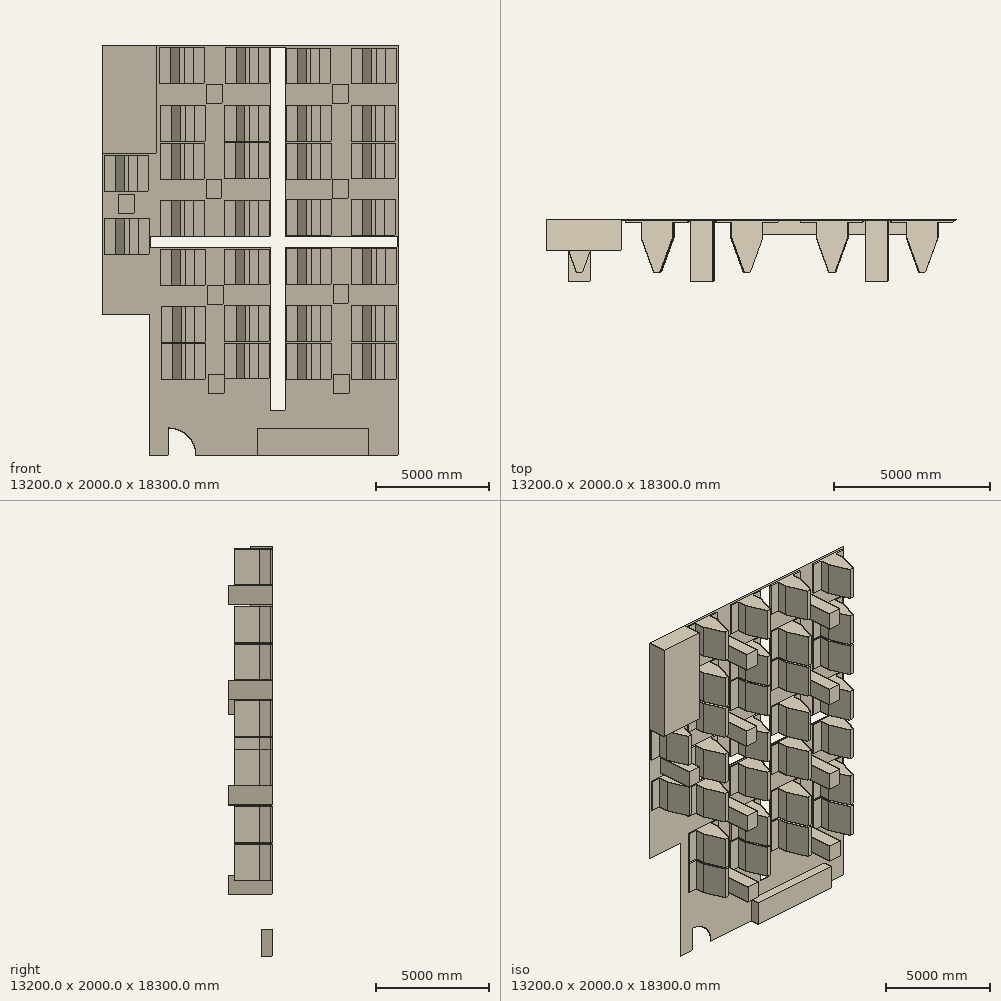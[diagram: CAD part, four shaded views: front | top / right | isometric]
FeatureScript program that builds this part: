
annotation { "Feature Type Name" : "Feature", "Feature Type Description" : "" }
export const myFeature = defineFeature(function(context is Context, id is Id, definition is map)
    precondition{}
    {
        {
            var Q0;
            Q0=qCreatedBy(makeId("Front.planeOp"),FACE);
            var sketch = newSketch(context, id + "F0", { "sketchPlane" : qUnion([Q0])});
            skLineSegment(sketch, "E0.bottom", {"start": v(6600, -7800) * mm, "end": v(-4500, -7800) * mm});
            skLineSegment(sketch, "E0.top", {"start": v(6600, 7800) * mm, "end": v(-6600, 7800) * mm});
            skLineSegment(sketch, "E0.left", {"start": v(6600, -7800) * mm, "end": v(6600, 7800) * mm});
            skLineSegment(sketch, "E0.right", {"start": v(-6600, -4200) * mm, "end": v(-6600, 7800) * mm});
            skPoint(sketch, "E0.middle", {"position": v(0, 0) * mm});
            skLineSegment(sketch, "E1.right", {"start": v(6599.52, -10500) * mm, "end": v(6599.52, -10500.52) * mm});
            skLineSegment(sketch, "E2", {"start": v(-4200, 7800) * mm, "end": v(-4200, 3000) * mm});
            skLineSegment(sketch, "E3", {"start": v(-4200, 3000) * mm, "end": v(-6600, 3000) * mm});
            skPoint(sketch, "E4", {"position": v(-6600, -4200) * mm});
            skLineSegment(sketch, "E5", {"start": v(-6600, -4200) * mm, "end": v(-4500, -4200) * mm});
            skLineSegment(sketch, "E6", {"start": v(-4500, -4200) * mm, "end": v(-4500, -10500) * mm});
            skPoint(sketch, "E7.orphan", {"position": v(-4500, -10500) * mm});
            skLineSegment(sketch, "E8", {"start": v(-4500, -10500) * mm, "end": v(6599.52, -10500) * mm});
            skLineSegment(sketch, "E9", {"start": v(6599.52, -10500) * mm, "end": v(6600, -7800) * mm});
            skLineSegment(sketch, "E10.bottom", {"start": v(-4048.74, 7699.43) * mm, "end": v(-2048.74, 7699.43) * mm});
            skLineSegment(sketch, "E10.top", {"start": v(-4048.74, 6099.43) * mm, "end": v(-2048.74, 6099.43) * mm});
            skLineSegment(sketch, "E10.left", {"start": v(-4048.74, 7699.43) * mm, "end": v(-4048.74, 6099.43) * mm});
            skLineSegment(sketch, "E10.right", {"start": v(-2048.74, 7699.43) * mm, "end": v(-2048.74, 6099.43) * mm});
            skLineSegment(sketch, "E11", {"start": v(-3548.74, 7699.43) * mm, "end": v(-3548.74, 6099.43) * mm});
            skLineSegment(sketch, "E12", {"start": v(-2548.74, 7699.43) * mm, "end": v(-2548.74, 6099.43) * mm});
            skLineSegment(sketch, "E13.bottom", {"start": v(-1955.3, 6065.3) * mm, "end": v(-1255.3, 6065.3) * mm});
            skLineSegment(sketch, "E13.top", {"start": v(-1955.3, 5215.3) * mm, "end": v(-1255.3, 5215.3) * mm});
            skLineSegment(sketch, "E13.left", {"start": v(-1955.3, 6065.3) * mm, "end": v(-1955.3, 5215.3) * mm});
            skLineSegment(sketch, "E13.right", {"start": v(-1255.3, 6065.3) * mm, "end": v(-1255.3, 5215.3) * mm});
            skLineSegment(sketch, "E14.bottom", {"start": v(-1133.47, 7702.4) * mm, "end": v(866.53, 7702.4) * mm});
            skLineSegment(sketch, "E14.top", {"start": v(-1133.47, 6102.4) * mm, "end": v(866.53, 6102.4) * mm});
            skLineSegment(sketch, "E14.left", {"start": v(-1133.47, 7702.4) * mm, "end": v(-1133.47, 6102.4) * mm});
            skLineSegment(sketch, "E14.right", {"start": v(866.53, 7702.4) * mm, "end": v(866.53, 6102.4) * mm});
            skLineSegment(sketch, "E15", {"start": v(-633.47, 7702.4) * mm, "end": v(-633.47, 6102.4) * mm});
            skLineSegment(sketch, "E16", {"start": v(366.53, 7702.4) * mm, "end": v(366.53, 6102.4) * mm});
            skLineSegment(sketch, "E17.bottom", {"start": v(-4021.77, 5133.48) * mm, "end": v(-2021.77, 5133.48) * mm});
            skLineSegment(sketch, "E17.top", {"start": v(-4021.77, 3533.48) * mm, "end": v(-2021.77, 3533.48) * mm});
            skLineSegment(sketch, "E17.left", {"start": v(-4021.77, 5133.48) * mm, "end": v(-4021.77, 3533.48) * mm});
            skLineSegment(sketch, "E17.right", {"start": v(-2021.77, 5133.48) * mm, "end": v(-2021.77, 3533.48) * mm});
            skLineSegment(sketch, "E18", {"start": v(-3521.77, 5133.48) * mm, "end": v(-3521.77, 3533.48) * mm});
            skLineSegment(sketch, "E19", {"start": v(-2521.77, 5133.48) * mm, "end": v(-2521.77, 3533.48) * mm});
            skLineSegment(sketch, "E20.bottom", {"start": v(-1146.79, 5133.48) * mm, "end": v(853.21, 5133.48) * mm});
            skLineSegment(sketch, "E20.top", {"start": v(-1146.79, 3533.48) * mm, "end": v(853.21, 3533.48) * mm});
            skLineSegment(sketch, "E20.left", {"start": v(-1146.79, 5133.48) * mm, "end": v(-1146.79, 3533.48) * mm});
            skLineSegment(sketch, "E20.right", {"start": v(853.21, 5133.48) * mm, "end": v(853.21, 3533.48) * mm});
            skLineSegment(sketch, "E21", {"start": v(-646.79, 5133.48) * mm, "end": v(-646.79, 3533.48) * mm});
            skLineSegment(sketch, "E22", {"start": v(353.21, 5133.48) * mm, "end": v(353.21, 3533.48) * mm});
            skLineSegment(sketch, "E23.bottom", {"start": v(1588.8, 7683.2) * mm, "end": v(3588.8, 7683.2) * mm});
            skLineSegment(sketch, "E23.top", {"start": v(1588.8, 6083.2) * mm, "end": v(3588.8, 6083.2) * mm});
            skLineSegment(sketch, "E23.left", {"start": v(1588.8, 7683.2) * mm, "end": v(1588.8, 6083.2) * mm});
            skLineSegment(sketch, "E23.right", {"start": v(3588.8, 7683.2) * mm, "end": v(3588.8, 6083.2) * mm});
            skLineSegment(sketch, "E24", {"start": v(2088.8, 7683.2) * mm, "end": v(2088.8, 6083.2) * mm});
            skLineSegment(sketch, "E25", {"start": v(3088.8, 7683.2) * mm, "end": v(3088.8, 6083.2) * mm});
            skLineSegment(sketch, "E26.bottom", {"start": v(3682.23, 6049.07) * mm, "end": v(4382.23, 6049.07) * mm});
            skLineSegment(sketch, "E26.top", {"start": v(3682.23, 5199.07) * mm, "end": v(4382.23, 5199.07) * mm});
            skLineSegment(sketch, "E26.left", {"start": v(3682.23, 6049.07) * mm, "end": v(3682.23, 5199.07) * mm});
            skLineSegment(sketch, "E26.right", {"start": v(4382.23, 6049.07) * mm, "end": v(4382.23, 5199.07) * mm});
            skLineSegment(sketch, "E27.bottom", {"start": v(4504.07, 7686.17) * mm, "end": v(6504.07, 7686.17) * mm});
            skLineSegment(sketch, "E27.top", {"start": v(4504.07, 6086.17) * mm, "end": v(6504.07, 6086.17) * mm});
            skLineSegment(sketch, "E27.left", {"start": v(4504.07, 7686.17) * mm, "end": v(4504.07, 6086.17) * mm});
            skLineSegment(sketch, "E27.right", {"start": v(6504.07, 7686.17) * mm, "end": v(6504.07, 6086.17) * mm});
            skLineSegment(sketch, "E28", {"start": v(5004.07, 7686.17) * mm, "end": v(5004.07, 6086.17) * mm});
            skLineSegment(sketch, "E29", {"start": v(6004.07, 7686.17) * mm, "end": v(6004.07, 6086.17) * mm});
            skLineSegment(sketch, "E30.bottom", {"start": v(1615.76, 5117.25) * mm, "end": v(3615.76, 5117.25) * mm});
            skLineSegment(sketch, "E30.top", {"start": v(1615.76, 3517.25) * mm, "end": v(3615.76, 3517.25) * mm});
            skLineSegment(sketch, "E30.left", {"start": v(1615.76, 5117.25) * mm, "end": v(1615.76, 3517.25) * mm});
            skLineSegment(sketch, "E30.right", {"start": v(3615.76, 5117.25) * mm, "end": v(3615.76, 3517.25) * mm});
            skLineSegment(sketch, "E31", {"start": v(2115.76, 5117.25) * mm, "end": v(2115.76, 3517.25) * mm});
            skLineSegment(sketch, "E32", {"start": v(3115.76, 5117.25) * mm, "end": v(3115.76, 3517.25) * mm});
            skLineSegment(sketch, "E33.bottom", {"start": v(4490.75, 5117.25) * mm, "end": v(6490.75, 5117.25) * mm});
            skLineSegment(sketch, "E33.top", {"start": v(4490.75, 3517.25) * mm, "end": v(6490.75, 3517.25) * mm});
            skLineSegment(sketch, "E33.left", {"start": v(4490.75, 5117.25) * mm, "end": v(4490.75, 3517.25) * mm});
            skLineSegment(sketch, "E33.right", {"start": v(6490.75, 5117.25) * mm, "end": v(6490.75, 3517.25) * mm});
            skLineSegment(sketch, "E34", {"start": v(4990.75, 5117.25) * mm, "end": v(4990.75, 3517.25) * mm});
            skLineSegment(sketch, "E35", {"start": v(5990.75, 5117.25) * mm, "end": v(5990.75, 3517.25) * mm});
            skLineSegment(sketch, "E36.bottom", {"start": v(1612.08, 3432.33) * mm, "end": v(3612.08, 3432.33) * mm});
            skLineSegment(sketch, "E36.top", {"start": v(1612.08, 1832.33) * mm, "end": v(3612.08, 1832.33) * mm});
            skLineSegment(sketch, "E36.left", {"start": v(1612.08, 3432.33) * mm, "end": v(1612.08, 1832.33) * mm});
            skLineSegment(sketch, "E36.right", {"start": v(3612.08, 3432.33) * mm, "end": v(3612.08, 1832.33) * mm});
            skLineSegment(sketch, "E37", {"start": v(2112.08, 3432.33) * mm, "end": v(2112.08, 1832.33) * mm});
            skLineSegment(sketch, "E38", {"start": v(3112.08, 3432.33) * mm, "end": v(3112.08, 1832.33) * mm});
            skLineSegment(sketch, "E39.bottom", {"start": v(3677.87, 1839.67) * mm, "end": v(4377.87, 1839.67) * mm});
            skLineSegment(sketch, "E39.top", {"start": v(3677.87, 989.67) * mm, "end": v(4377.87, 989.67) * mm});
            skLineSegment(sketch, "E39.left", {"start": v(3677.87, 1839.67) * mm, "end": v(3677.87, 989.67) * mm});
            skLineSegment(sketch, "E39.right", {"start": v(4377.87, 1839.67) * mm, "end": v(4377.87, 989.67) * mm});
            skLineSegment(sketch, "E40.bottom", {"start": v(4492.8, 3442.2) * mm, "end": v(6492.8, 3442.2) * mm});
            skLineSegment(sketch, "E40.top", {"start": v(4492.8, 1842.2) * mm, "end": v(6492.8, 1842.2) * mm});
            skLineSegment(sketch, "E40.left", {"start": v(4492.8, 3442.2) * mm, "end": v(4492.8, 1842.2) * mm});
            skLineSegment(sketch, "E40.right", {"start": v(6492.8, 3442.2) * mm, "end": v(6492.8, 1842.2) * mm});
            skLineSegment(sketch, "E41", {"start": v(4992.8, 3442.2) * mm, "end": v(4992.8, 1842.2) * mm});
            skLineSegment(sketch, "E42", {"start": v(5992.8, 3442.2) * mm, "end": v(5992.8, 1842.2) * mm});
            skLineSegment(sketch, "E43.bottom", {"start": v(1611.4, 907.84) * mm, "end": v(3611.4, 907.84) * mm});
            skLineSegment(sketch, "E43.top", {"start": v(1611.4, -692.16) * mm, "end": v(3611.4, -692.16) * mm});
            skLineSegment(sketch, "E43.left", {"start": v(1611.4, 907.84) * mm, "end": v(1611.4, -692.16) * mm});
            skLineSegment(sketch, "E43.right", {"start": v(3611.4, 907.84) * mm, "end": v(3611.4, -692.16) * mm});
            skLineSegment(sketch, "E44", {"start": v(2111.4, 907.84) * mm, "end": v(2111.4, -692.16) * mm});
            skLineSegment(sketch, "E45", {"start": v(3111.4, 907.84) * mm, "end": v(3111.4, -692.16) * mm});
            skLineSegment(sketch, "E46.bottom", {"start": v(4486.39, 907.84) * mm, "end": v(6486.39, 907.84) * mm});
            skLineSegment(sketch, "E46.top", {"start": v(4486.39, -692.16) * mm, "end": v(6486.39, -692.16) * mm});
            skLineSegment(sketch, "E46.left", {"start": v(4486.39, 907.84) * mm, "end": v(4486.39, -692.16) * mm});
            skLineSegment(sketch, "E46.right", {"start": v(6486.39, 907.84) * mm, "end": v(6486.39, -692.16) * mm});
            skLineSegment(sketch, "E47", {"start": v(4986.39, 907.84) * mm, "end": v(4986.39, -692.16) * mm});
            skLineSegment(sketch, "E48", {"start": v(5986.39, 907.84) * mm, "end": v(5986.39, -692.16) * mm});
            skLineSegment(sketch, "E49.bottom", {"start": v(-4031.74, 3435.59) * mm, "end": v(-2031.74, 3435.59) * mm});
            skLineSegment(sketch, "E49.top", {"start": v(-4031.74, 1835.59) * mm, "end": v(-2031.74, 1835.59) * mm});
            skLineSegment(sketch, "E49.left", {"start": v(-4031.74, 3435.59) * mm, "end": v(-4031.74, 1835.59) * mm});
            skLineSegment(sketch, "E49.right", {"start": v(-2031.74, 3435.59) * mm, "end": v(-2031.74, 1835.59) * mm});
            skLineSegment(sketch, "E50", {"start": v(-3531.74, 3435.59) * mm, "end": v(-3531.74, 1835.59) * mm});
            skLineSegment(sketch, "E51", {"start": v(-2531.74, 3435.59) * mm, "end": v(-2531.74, 1835.59) * mm});
            skLineSegment(sketch, "E52.bottom", {"start": v(-1972.86, 1822.2) * mm, "end": v(-1272.86, 1822.2) * mm});
            skLineSegment(sketch, "E52.top", {"start": v(-1972.86, 972.2) * mm, "end": v(-1272.86, 972.2) * mm});
            skLineSegment(sketch, "E52.left", {"start": v(-1972.86, 1822.2) * mm, "end": v(-1972.86, 972.2) * mm});
            skLineSegment(sketch, "E52.right", {"start": v(-1272.86, 1822.2) * mm, "end": v(-1272.86, 972.2) * mm});
            skLineSegment(sketch, "E53.bottom", {"start": v(-1151.02, 3459.29) * mm, "end": v(848.98, 3459.29) * mm});
            skLineSegment(sketch, "E53.top", {"start": v(-1151.02, 1859.29) * mm, "end": v(848.98, 1859.29) * mm});
            skLineSegment(sketch, "E53.left", {"start": v(-1151.02, 3459.29) * mm, "end": v(-1151.02, 1859.29) * mm});
            skLineSegment(sketch, "E53.right", {"start": v(848.98, 3459.29) * mm, "end": v(848.98, 1859.29) * mm});
            skLineSegment(sketch, "E54", {"start": v(-651.02, 3459.29) * mm, "end": v(-651.02, 1859.29) * mm});
            skLineSegment(sketch, "E55", {"start": v(348.98, 3459.29) * mm, "end": v(348.98, 1859.29) * mm});
            skLineSegment(sketch, "E56.bottom", {"start": v(-4039.33, 890.37) * mm, "end": v(-2039.33, 890.37) * mm});
            skLineSegment(sketch, "E56.top", {"start": v(-4039.33, -709.63) * mm, "end": v(-2039.33, -709.63) * mm});
            skLineSegment(sketch, "E56.left", {"start": v(-4039.33, 890.37) * mm, "end": v(-4039.33, -709.63) * mm});
            skLineSegment(sketch, "E56.right", {"start": v(-2039.33, 890.37) * mm, "end": v(-2039.33, -709.63) * mm});
            skLineSegment(sketch, "E57", {"start": v(-3539.33, 890.37) * mm, "end": v(-3539.33, -709.63) * mm});
            skLineSegment(sketch, "E58", {"start": v(-2539.33, 890.37) * mm, "end": v(-2539.33, -709.63) * mm});
            skLineSegment(sketch, "E59.bottom", {"start": v(-1164.34, 890.37) * mm, "end": v(835.66, 890.37) * mm});
            skLineSegment(sketch, "E59.top", {"start": v(-1164.34, -709.63) * mm, "end": v(835.66, -709.63) * mm});
            skLineSegment(sketch, "E59.left", {"start": v(-1164.34, 890.37) * mm, "end": v(-1164.34, -709.63) * mm});
            skLineSegment(sketch, "E59.right", {"start": v(835.66, 890.37) * mm, "end": v(835.66, -709.63) * mm});
            skLineSegment(sketch, "E60", {"start": v(-664.34, 890.37) * mm, "end": v(-664.34, -709.63) * mm});
            skLineSegment(sketch, "E61", {"start": v(335.66, 890.37) * mm, "end": v(335.66, -709.63) * mm});
            skLineSegment(sketch, "E62.bottom", {"start": v(1618.8, -1260.11) * mm, "end": v(3618.8, -1260.11) * mm});
            skLineSegment(sketch, "E62.top", {"start": v(1618.8, -2860.11) * mm, "end": v(3618.8, -2860.11) * mm});
            skLineSegment(sketch, "E62.left", {"start": v(1618.8, -1260.11) * mm, "end": v(1618.8, -2860.11) * mm});
            skLineSegment(sketch, "E62.right", {"start": v(3618.8, -1260.11) * mm, "end": v(3618.8, -2860.11) * mm});
            skLineSegment(sketch, "E63", {"start": v(2118.8, -1260.11) * mm, "end": v(2118.8, -2860.11) * mm});
            skLineSegment(sketch, "E64", {"start": v(3118.8, -1260.11) * mm, "end": v(3118.8, -2860.11) * mm});
            skLineSegment(sketch, "E65.bottom", {"start": v(3686.07, -2882.62) * mm, "end": v(4386.07, -2882.62) * mm});
            skLineSegment(sketch, "E65.top", {"start": v(3686.07, -3732.62) * mm, "end": v(4386.07, -3732.62) * mm});
            skLineSegment(sketch, "E65.left", {"start": v(3686.07, -2882.62) * mm, "end": v(3686.07, -3732.62) * mm});
            skLineSegment(sketch, "E65.right", {"start": v(4386.07, -2882.62) * mm, "end": v(4386.07, -3732.62) * mm});
            skLineSegment(sketch, "E66.bottom", {"start": v(4507.92, -1245.52) * mm, "end": v(6507.92, -1245.52) * mm});
            skLineSegment(sketch, "E66.top", {"start": v(4507.92, -2845.52) * mm, "end": v(6507.92, -2845.52) * mm});
            skLineSegment(sketch, "E66.left", {"start": v(4507.92, -1245.52) * mm, "end": v(4507.92, -2845.52) * mm});
            skLineSegment(sketch, "E66.right", {"start": v(6507.92, -1245.52) * mm, "end": v(6507.92, -2845.52) * mm});
            skLineSegment(sketch, "E67", {"start": v(5007.92, -1245.52) * mm, "end": v(5007.92, -2845.52) * mm});
            skLineSegment(sketch, "E68", {"start": v(6007.92, -1245.52) * mm, "end": v(6007.92, -2845.52) * mm});
            skLineSegment(sketch, "E69.bottom", {"start": v(1619.61, -3814.44) * mm, "end": v(3619.61, -3814.44) * mm});
            skLineSegment(sketch, "E69.top", {"start": v(1619.61, -5414.44) * mm, "end": v(3619.61, -5414.44) * mm});
            skLineSegment(sketch, "E69.left", {"start": v(1619.61, -3814.44) * mm, "end": v(1619.61, -5414.44) * mm});
            skLineSegment(sketch, "E69.right", {"start": v(3619.61, -3814.44) * mm, "end": v(3619.61, -5414.44) * mm});
            skLineSegment(sketch, "E70", {"start": v(2119.61, -3814.44) * mm, "end": v(2119.61, -5414.44) * mm});
            skLineSegment(sketch, "E71", {"start": v(3119.61, -3814.44) * mm, "end": v(3119.61, -5414.44) * mm});
            skLineSegment(sketch, "E72.bottom", {"start": v(4494.6, -3814.44) * mm, "end": v(6494.6, -3814.44) * mm});
            skLineSegment(sketch, "E72.top", {"start": v(4494.6, -5414.44) * mm, "end": v(6494.6, -5414.44) * mm});
            skLineSegment(sketch, "E72.left", {"start": v(4494.6, -3814.44) * mm, "end": v(4494.6, -5414.44) * mm});
            skLineSegment(sketch, "E72.right", {"start": v(6494.6, -3814.44) * mm, "end": v(6494.6, -5414.44) * mm});
            skLineSegment(sketch, "E73", {"start": v(4994.6, -3814.44) * mm, "end": v(4994.6, -5414.44) * mm});
            skLineSegment(sketch, "E74", {"start": v(5994.6, -3814.44) * mm, "end": v(5994.6, -5414.44) * mm});
            skLineSegment(sketch, "E75.bottom", {"start": v(-4019.91, -1290.57) * mm, "end": v(-2019.91, -1290.57) * mm});
            skLineSegment(sketch, "E75.top", {"start": v(-4019.91, -2890.57) * mm, "end": v(-2019.91, -2890.57) * mm});
            skLineSegment(sketch, "E75.left", {"start": v(-4019.91, -1290.57) * mm, "end": v(-4019.91, -2890.57) * mm});
            skLineSegment(sketch, "E75.right", {"start": v(-2019.91, -1290.57) * mm, "end": v(-2019.91, -2890.57) * mm});
            skLineSegment(sketch, "E76", {"start": v(-3519.91, -1290.57) * mm, "end": v(-3519.91, -2890.57) * mm});
            skLineSegment(sketch, "E77", {"start": v(-2519.91, -1290.57) * mm, "end": v(-2519.91, -2890.57) * mm});
            skLineSegment(sketch, "E78.bottom", {"start": v(-1926.48, -2924.7) * mm, "end": v(-1226.48, -2924.7) * mm});
            skLineSegment(sketch, "E78.top", {"start": v(-1926.48, -3774.7) * mm, "end": v(-1226.48, -3774.7) * mm});
            skLineSegment(sketch, "E78.left", {"start": v(-1926.48, -2924.7) * mm, "end": v(-1926.48, -3774.7) * mm});
            skLineSegment(sketch, "E78.right", {"start": v(-1226.48, -2924.7) * mm, "end": v(-1226.48, -3774.7) * mm});
            skLineSegment(sketch, "E79.bottom", {"start": v(-1156.94, -1287.6) * mm, "end": v(843.06, -1287.6) * mm});
            skLineSegment(sketch, "E79.top", {"start": v(-1156.94, -2887.6) * mm, "end": v(843.06, -2887.6) * mm});
            skLineSegment(sketch, "E79.left", {"start": v(-1156.94, -1287.6) * mm, "end": v(-1156.94, -2887.6) * mm});
            skLineSegment(sketch, "E79.right", {"start": v(843.06, -1287.6) * mm, "end": v(843.06, -2887.6) * mm});
            skLineSegment(sketch, "E80", {"start": v(-656.94, -1287.6) * mm, "end": v(-656.94, -2887.6) * mm});
            skLineSegment(sketch, "E81", {"start": v(343.06, -1287.6) * mm, "end": v(343.06, -2887.6) * mm});
            skLineSegment(sketch, "E82.bottom", {"start": v(-3992.94, -3856.53) * mm, "end": v(-1992.94, -3856.53) * mm});
            skLineSegment(sketch, "E82.top", {"start": v(-3992.94, -5456.53) * mm, "end": v(-1992.94, -5456.53) * mm});
            skLineSegment(sketch, "E82.left", {"start": v(-3992.94, -3856.53) * mm, "end": v(-3992.94, -5456.53) * mm});
            skLineSegment(sketch, "E82.right", {"start": v(-1992.94, -3856.53) * mm, "end": v(-1992.94, -5456.53) * mm});
            skLineSegment(sketch, "E83", {"start": v(-3492.94, -3856.53) * mm, "end": v(-3492.94, -5456.53) * mm});
            skLineSegment(sketch, "E84", {"start": v(-2492.94, -3856.53) * mm, "end": v(-2492.94, -5456.53) * mm});
            skLineSegment(sketch, "E85.bottom", {"start": v(-1141.2, -3810.03) * mm, "end": v(858.8, -3810.03) * mm});
            skLineSegment(sketch, "E85.top", {"start": v(-1141.2, -5410.03) * mm, "end": v(858.8, -5410.03) * mm});
            skLineSegment(sketch, "E85.left", {"start": v(-1141.2, -3810.03) * mm, "end": v(-1141.2, -5410.03) * mm});
            skLineSegment(sketch, "E85.right", {"start": v(858.8, -3810.03) * mm, "end": v(858.8, -5410.03) * mm});
            skLineSegment(sketch, "E86", {"start": v(-641.2, -3810.03) * mm, "end": v(-641.2, -5410.03) * mm});
            skLineSegment(sketch, "E87", {"start": v(358.8, -3810.03) * mm, "end": v(358.8, -5410.03) * mm});
            skLineSegment(sketch, "E88.bottom", {"start": v(-6536.37, 2901.13) * mm, "end": v(-4536.37, 2901.13) * mm});
            skLineSegment(sketch, "E88.top", {"start": v(-6536.37, 1301.13) * mm, "end": v(-4536.37, 1301.13) * mm});
            skLineSegment(sketch, "E88.left", {"start": v(-6536.37, 2901.13) * mm, "end": v(-6536.37, 1301.13) * mm});
            skLineSegment(sketch, "E88.right", {"start": v(-4536.37, 2901.13) * mm, "end": v(-4536.37, 1301.13) * mm});
            skLineSegment(sketch, "E89", {"start": v(-6036.37, 2901.13) * mm, "end": v(-6036.37, 1301.13) * mm});
            skLineSegment(sketch, "E90", {"start": v(-5036.37, 2901.13) * mm, "end": v(-5036.37, 1301.13) * mm});
            skLineSegment(sketch, "E91.bottom", {"start": v(-5894.25, 1149.52) * mm, "end": v(-5194.25, 1149.52) * mm});
            skLineSegment(sketch, "E91.top", {"start": v(-5894.25, 299.52) * mm, "end": v(-5194.25, 299.52) * mm});
            skLineSegment(sketch, "E91.left", {"start": v(-5894.25, 1149.52) * mm, "end": v(-5894.25, 299.52) * mm});
            skLineSegment(sketch, "E91.right", {"start": v(-5194.25, 1149.52) * mm, "end": v(-5194.25, 299.52) * mm});
            skLineSegment(sketch, "E92.bottom", {"start": v(-6509.4, 72.56) * mm, "end": v(-4509.4, 72.56) * mm});
            skLineSegment(sketch, "E92.top", {"start": v(-6509.4, -1527.44) * mm, "end": v(-4509.4, -1527.44) * mm});
            skLineSegment(sketch, "E92.left", {"start": v(-6509.4, 72.56) * mm, "end": v(-6509.4, -1527.44) * mm});
            skLineSegment(sketch, "E92.right", {"start": v(-4509.4, 72.56) * mm, "end": v(-4509.4, -1527.44) * mm});
            skLineSegment(sketch, "E93", {"start": v(-6009.4, 72.56) * mm, "end": v(-6009.4, -1527.44) * mm});
            skLineSegment(sketch, "E94", {"start": v(-5009.4, 72.56) * mm, "end": v(-5009.4, -1527.44) * mm});
            skLineSegment(sketch, "E95.bottom", {"start": v(-3994.24, -5520.89) * mm, "end": v(-1994.24, -5520.89) * mm});
            skLineSegment(sketch, "E95.top", {"start": v(-3994.24, -7120.89) * mm, "end": v(-1994.24, -7120.89) * mm});
            skLineSegment(sketch, "E95.left", {"start": v(-3994.24, -5520.89) * mm, "end": v(-3994.24, -7120.89) * mm});
            skLineSegment(sketch, "E95.right", {"start": v(-1994.24, -5520.89) * mm, "end": v(-1994.24, -7120.89) * mm});
            skLineSegment(sketch, "E96", {"start": v(-3494.24, -5520.89) * mm, "end": v(-3494.24, -7120.89) * mm});
            skLineSegment(sketch, "E97", {"start": v(-2494.24, -5520.89) * mm, "end": v(-2494.24, -7120.89) * mm});
            skLineSegment(sketch, "E98.bottom", {"start": v(-1876.15, -6899.35) * mm, "end": v(-1176.15, -6899.35) * mm});
            skLineSegment(sketch, "E98.top", {"start": v(-1876.15, -7749.35) * mm, "end": v(-1176.15, -7749.35) * mm});
            skLineSegment(sketch, "E98.left", {"start": v(-1876.15, -6899.35) * mm, "end": v(-1876.15, -7749.35) * mm});
            skLineSegment(sketch, "E98.right", {"start": v(-1176.15, -6899.35) * mm, "end": v(-1176.15, -7749.35) * mm});
            skLineSegment(sketch, "E99.bottom", {"start": v(-1145.97, -5479.65) * mm, "end": v(854.03, -5479.65) * mm});
            skLineSegment(sketch, "E99.top", {"start": v(-1145.97, -7079.65) * mm, "end": v(854.03, -7079.65) * mm});
            skLineSegment(sketch, "E99.left", {"start": v(-1145.97, -5479.65) * mm, "end": v(-1145.97, -7079.65) * mm});
            skLineSegment(sketch, "E99.right", {"start": v(854.03, -5479.65) * mm, "end": v(854.03, -7079.65) * mm});
            skLineSegment(sketch, "E100", {"start": v(-645.97, -5479.65) * mm, "end": v(-645.97, -7079.65) * mm});
            skLineSegment(sketch, "E101", {"start": v(354.03, -5479.65) * mm, "end": v(354.03, -7079.65) * mm});
            skLineSegment(sketch, "E102.bottom", {"start": v(1618.38, -5506.92) * mm, "end": v(3618.38, -5506.92) * mm});
            skLineSegment(sketch, "E102.top", {"start": v(1618.38, -7106.92) * mm, "end": v(3618.38, -7106.92) * mm});
            skLineSegment(sketch, "E102.left", {"start": v(1618.38, -5506.92) * mm, "end": v(1618.38, -7106.92) * mm});
            skLineSegment(sketch, "E102.right", {"start": v(3618.38, -5506.92) * mm, "end": v(3618.38, -7106.92) * mm});
            skLineSegment(sketch, "E103", {"start": v(2118.38, -5506.92) * mm, "end": v(2118.38, -7106.92) * mm});
            skLineSegment(sketch, "E104", {"start": v(3118.38, -5506.92) * mm, "end": v(3118.38, -7106.92) * mm});
            skLineSegment(sketch, "E105.bottom", {"start": v(3710.25, -6893.6) * mm, "end": v(4410.25, -6893.6) * mm});
            skLineSegment(sketch, "E105.top", {"start": v(3710.25, -7743.6) * mm, "end": v(4410.25, -7743.6) * mm});
            skLineSegment(sketch, "E105.left", {"start": v(3710.25, -6893.6) * mm, "end": v(3710.25, -7743.6) * mm});
            skLineSegment(sketch, "E105.right", {"start": v(4410.25, -6893.6) * mm, "end": v(4410.25, -7743.6) * mm});
            skLineSegment(sketch, "E106.bottom", {"start": v(4496.66, -5508.06) * mm, "end": v(6496.66, -5508.06) * mm});
            skLineSegment(sketch, "E106.top", {"start": v(4496.66, -7108.06) * mm, "end": v(6496.66, -7108.06) * mm});
            skLineSegment(sketch, "E106.left", {"start": v(4496.66, -5508.06) * mm, "end": v(4496.66, -7108.06) * mm});
            skLineSegment(sketch, "E106.right", {"start": v(6496.66, -5508.06) * mm, "end": v(6496.66, -7108.06) * mm});
            skLineSegment(sketch, "E107", {"start": v(4996.66, -5508.06) * mm, "end": v(4996.66, -7108.06) * mm});
            skLineSegment(sketch, "E108", {"start": v(5996.66, -5508.06) * mm, "end": v(5996.66, -7108.06) * mm});
            skLineSegment(sketch, "E109.bottom", {"start": v(322.54, -9289.8) * mm, "end": v(5287.7, -9289.8) * mm});
            skLineSegment(sketch, "E109.top", {"start": v(322.54, -10500) * mm, "end": v(5287.7, -10500) * mm});
            skLineSegment(sketch, "E109.left", {"start": v(322.54, -9289.8) * mm, "end": v(322.54, -10500) * mm});
            skLineSegment(sketch, "E109.right", {"start": v(5287.7, -9289.8) * mm, "end": v(5287.7, -10500) * mm});
            skLineSegment(sketch, "E110", {"start": v(-3665.22, -9270.26) * mm, "end": v(-3665.22, -10500) * mm});
            skArc(sketch, "E111", {"start": v(-3665.22, -9270.26) * mm, "mid": v(-2795.66, -9630.44) * mm, "end": v(-2435.48, -10500) * mm});
            skLineSegment(sketch, "E112.bottom", {"start": v(912.9, 7702.4) * mm, "end": v(1572.64, 7702.4) * mm});
            skLineSegment(sketch, "E112.top", {"start": v(912.9, -8513.66) * mm, "end": v(1572.64, -8513.66) * mm});
            skLineSegment(sketch, "E112.left", {"start": v(912.9, 7702.4) * mm, "end": v(912.9, -732.9) * mm});
            skLineSegment(sketch, "E112.right", {"start": v(1572.64, 7702.4) * mm, "end": v(1572.64, -732.9) * mm});
            skLineSegment(sketch, "E113.bottom", {"start": v(-4460.78, -732.9) * mm, "end": v(912.9, -732.9) * mm});
            skLineSegment(sketch, "E113.top", {"start": v(-4460.78, -1212.28) * mm, "end": v(912.9, -1212.28) * mm});
            skLineSegment(sketch, "E113.left", {"start": v(-4460.78, -732.9) * mm, "end": v(-4460.78, -1212.28) * mm});
            skLineSegment(sketch, "E113.right", {"start": v(6553.67, -732.9) * mm, "end": v(6553.67, -1212.28) * mm});
            skLineSegment(sketch, "E114.trimOffspring", {"start": v(912.9, -1212.28) * mm, "end": v(912.9, -8513.66) * mm});
            skLineSegment(sketch, "E115.trimOffspring", {"start": v(1572.64, -732.9) * mm, "end": v(6553.67, -732.9) * mm});
            skLineSegment(sketch, "E116.trimOffspring", {"start": v(1572.64, -1212.28) * mm, "end": v(6553.67, -1212.28) * mm});
            skLineSegment(sketch, "E117.trimOffspring", {"start": v(1572.64, -1212.28) * mm, "end": v(1572.64, -8513.66) * mm});
            skSolve(sketch);
        }
        {
            var Q0;
            {var subQ138=sQuery(id+"F0.wireOp",EDGE,"E0.bottom");Q0=makeQuery(id+"F0.imprint","IMPRINT",FACE,{"disambiguationData":[TD([[makeQuery(id+"F0.imprint","IMPRINT",EDGE,{"derivedFrom":subQ138}),-1.0]])]});}
            var Q1;
            {var subQ0=sQuery(id+"F0.wireOp",EDGE,"E0.bottom");Q1=makeQuery(id+"F0.imprint","IMPRINT",FACE,{"disambiguationData":[TD([[makeQuery(id+"F0.imprint","IMPRINT",EDGE,{"derivedFrom":subQ0}),1.0]])]});}
            extrude(context, id + "F1", {"entities" : qUnion([Q0, Q1]), "depth" : 25 * mm, "offsetDistance" : 25 * mm});
        }
        {
            var Q0;
            {var subQ3=sQuery(id+"F0.wireOp",EDGE,"E2");Q0=makeQuery(id+"F0.imprint","IMPRINT",FACE,{"disambiguationData":[TD([[makeQuery(id+"F0.imprint","IMPRINT",EDGE,{"derivedFrom":subQ3}),-1.0]])]});}
            extrude(context, id + "F2", {"entities" : qUnion([Q0]), "operationType" : NewBodyOperationType.ADD, "depth" : 1000 * mm, "offsetDistance" : 25 * mm});
        }
        {
            var Q0;
            {var subQ0=sQuery(id+"F0.wireOp",EDGE,"E11");Q0=makeQuery(id+"F0.imprint","IMPRINT",FACE,{"disambiguationData":[TD([[makeQuery(id+"F0.imprint","IMPRINT",EDGE,{"derivedFrom":subQ0}),1.0]])]});}
            var Q1;
            {var subQ0=sQuery(id+"F0.wireOp",EDGE,"E15");Q1=makeQuery(id+"F0.imprint","IMPRINT",FACE,{"disambiguationData":[TD([[makeQuery(id+"F0.imprint","IMPRINT",EDGE,{"derivedFrom":subQ0}),1.0]])]});}
            var Q2;
            {var subQ0=sQuery(id+"F0.wireOp",EDGE,"E24");Q2=makeQuery(id+"F0.imprint","IMPRINT",FACE,{"disambiguationData":[TD([[makeQuery(id+"F0.imprint","IMPRINT",EDGE,{"derivedFrom":subQ0}),1.0]])]});}
            var Q3;
            {var subQ0=sQuery(id+"F0.wireOp",EDGE,"E28");Q3=makeQuery(id+"F0.imprint","IMPRINT",FACE,{"disambiguationData":[TD([[makeQuery(id+"F0.imprint","IMPRINT",EDGE,{"derivedFrom":subQ0}),1.0]])]});}
            var Q4;
            {var subQ0=sQuery(id+"F0.wireOp",EDGE,"E34");Q4=makeQuery(id+"F0.imprint","IMPRINT",FACE,{"disambiguationData":[TD([[makeQuery(id+"F0.imprint","IMPRINT",EDGE,{"derivedFrom":subQ0}),1.0]])]});}
            var Q5;
            {var subQ0=sQuery(id+"F0.wireOp",EDGE,"E31");Q5=makeQuery(id+"F0.imprint","IMPRINT",FACE,{"disambiguationData":[TD([[makeQuery(id+"F0.imprint","IMPRINT",EDGE,{"derivedFrom":subQ0}),1.0]])]});}
            var Q6;
            {var subQ0=sQuery(id+"F0.wireOp",EDGE,"E37");Q6=makeQuery(id+"F0.imprint","IMPRINT",FACE,{"disambiguationData":[TD([[makeQuery(id+"F0.imprint","IMPRINT",EDGE,{"derivedFrom":subQ0}),1.0]])]});}
            var Q7;
            {var subQ0=sQuery(id+"F0.wireOp",EDGE,"E41");Q7=makeQuery(id+"F0.imprint","IMPRINT",FACE,{"disambiguationData":[TD([[makeQuery(id+"F0.imprint","IMPRINT",EDGE,{"derivedFrom":subQ0}),1.0]])]});}
            var Q8;
            {var subQ0=sQuery(id+"F0.wireOp",EDGE,"E54");Q8=makeQuery(id+"F0.imprint","IMPRINT",FACE,{"disambiguationData":[TD([[makeQuery(id+"F0.imprint","IMPRINT",EDGE,{"derivedFrom":subQ0}),1.0]])]});}
            var Q9;
            {var subQ0=sQuery(id+"F0.wireOp",EDGE,"E21");Q9=makeQuery(id+"F0.imprint","IMPRINT",FACE,{"disambiguationData":[TD([[makeQuery(id+"F0.imprint","IMPRINT",EDGE,{"derivedFrom":subQ0}),1.0]])]});}
            var Q10;
            {var subQ0=sQuery(id+"F0.wireOp",EDGE,"E18");Q10=makeQuery(id+"F0.imprint","IMPRINT",FACE,{"disambiguationData":[TD([[makeQuery(id+"F0.imprint","IMPRINT",EDGE,{"derivedFrom":subQ0}),1.0]])]});}
            var Q11;
            {var subQ0=sQuery(id+"F0.wireOp",EDGE,"E50");Q11=makeQuery(id+"F0.imprint","IMPRINT",FACE,{"disambiguationData":[TD([[makeQuery(id+"F0.imprint","IMPRINT",EDGE,{"derivedFrom":subQ0}),1.0]])]});}
            var Q12;
            {var subQ0=sQuery(id+"F0.wireOp",EDGE,"E89");Q12=makeQuery(id+"F0.imprint","IMPRINT",FACE,{"disambiguationData":[TD([[makeQuery(id+"F0.imprint","IMPRINT",EDGE,{"derivedFrom":subQ0}),1.0]])]});}
            var Q13;
            {var subQ0=sQuery(id+"F0.wireOp",EDGE,"E93");Q13=makeQuery(id+"F0.imprint","IMPRINT",FACE,{"disambiguationData":[TD([[makeQuery(id+"F0.imprint","IMPRINT",EDGE,{"derivedFrom":subQ0}),1.0]])]});}
            var Q14;
            {var subQ0=sQuery(id+"F0.wireOp",EDGE,"E57");Q14=makeQuery(id+"F0.imprint","IMPRINT",FACE,{"disambiguationData":[TD([[makeQuery(id+"F0.imprint","IMPRINT",EDGE,{"derivedFrom":subQ0}),1.0]])]});}
            var Q15;
            {var subQ0=sQuery(id+"F0.wireOp",EDGE,"E76");Q15=makeQuery(id+"F0.imprint","IMPRINT",FACE,{"disambiguationData":[TD([[makeQuery(id+"F0.imprint","IMPRINT",EDGE,{"derivedFrom":subQ0}),1.0]])]});}
            var Q16;
            {var subQ0=sQuery(id+"F0.wireOp",EDGE,"E80");Q16=makeQuery(id+"F0.imprint","IMPRINT",FACE,{"disambiguationData":[TD([[makeQuery(id+"F0.imprint","IMPRINT",EDGE,{"derivedFrom":subQ0}),1.0]])]});}
            var Q17;
            {var subQ0=sQuery(id+"F0.wireOp",EDGE,"E60");Q17=makeQuery(id+"F0.imprint","IMPRINT",FACE,{"disambiguationData":[TD([[makeQuery(id+"F0.imprint","IMPRINT",EDGE,{"derivedFrom":subQ0}),1.0]])]});}
            var Q18;
            {var subQ0=sQuery(id+"F0.wireOp",EDGE,"E44");Q18=makeQuery(id+"F0.imprint","IMPRINT",FACE,{"disambiguationData":[TD([[makeQuery(id+"F0.imprint","IMPRINT",EDGE,{"derivedFrom":subQ0}),1.0]])]});}
            var Q19;
            {var subQ0=sQuery(id+"F0.wireOp",EDGE,"E63");Q19=makeQuery(id+"F0.imprint","IMPRINT",FACE,{"disambiguationData":[TD([[makeQuery(id+"F0.imprint","IMPRINT",EDGE,{"derivedFrom":subQ0}),1.0]])]});}
            var Q20;
            {var subQ0=sQuery(id+"F0.wireOp",EDGE,"E67");Q20=makeQuery(id+"F0.imprint","IMPRINT",FACE,{"disambiguationData":[TD([[makeQuery(id+"F0.imprint","IMPRINT",EDGE,{"derivedFrom":subQ0}),1.0]])]});}
            var Q21;
            {var subQ0=sQuery(id+"F0.wireOp",EDGE,"E47");Q21=makeQuery(id+"F0.imprint","IMPRINT",FACE,{"disambiguationData":[TD([[makeQuery(id+"F0.imprint","IMPRINT",EDGE,{"derivedFrom":subQ0}),1.0]])]});}
            var Q22;
            {var subQ0=sQuery(id+"F0.wireOp",EDGE,"E73");Q22=makeQuery(id+"F0.imprint","IMPRINT",FACE,{"disambiguationData":[TD([[makeQuery(id+"F0.imprint","IMPRINT",EDGE,{"derivedFrom":subQ0}),1.0]])]});}
            var Q23;
            {var subQ0=sQuery(id+"F0.wireOp",EDGE,"E107");Q23=makeQuery(id+"F0.imprint","IMPRINT",FACE,{"disambiguationData":[TD([[makeQuery(id+"F0.imprint","IMPRINT",EDGE,{"derivedFrom":subQ0}),1.0]])]});}
            var Q24;
            {var subQ0=sQuery(id+"F0.wireOp",EDGE,"E103");Q24=makeQuery(id+"F0.imprint","IMPRINT",FACE,{"disambiguationData":[TD([[makeQuery(id+"F0.imprint","IMPRINT",EDGE,{"derivedFrom":subQ0}),1.0]])]});}
            var Q25;
            {var subQ0=sQuery(id+"F0.wireOp",EDGE,"E70");Q25=makeQuery(id+"F0.imprint","IMPRINT",FACE,{"disambiguationData":[TD([[makeQuery(id+"F0.imprint","IMPRINT",EDGE,{"derivedFrom":subQ0}),1.0]])]});}
            var Q26;
            {var subQ0=sQuery(id+"F0.wireOp",EDGE,"E86");Q26=makeQuery(id+"F0.imprint","IMPRINT",FACE,{"disambiguationData":[TD([[makeQuery(id+"F0.imprint","IMPRINT",EDGE,{"derivedFrom":subQ0}),1.0]])]});}
            var Q27;
            {var subQ0=sQuery(id+"F0.wireOp",EDGE,"E100");Q27=makeQuery(id+"F0.imprint","IMPRINT",FACE,{"disambiguationData":[TD([[makeQuery(id+"F0.imprint","IMPRINT",EDGE,{"derivedFrom":subQ0}),1.0]])]});}
            var Q28;
            {var subQ0=sQuery(id+"F0.wireOp",EDGE,"E96");Q28=makeQuery(id+"F0.imprint","IMPRINT",FACE,{"disambiguationData":[TD([[makeQuery(id+"F0.imprint","IMPRINT",EDGE,{"derivedFrom":subQ0}),1.0]])]});}
            var Q29;
            {var subQ0=sQuery(id+"F0.wireOp",EDGE,"E83");Q29=makeQuery(id+"F0.imprint","IMPRINT",FACE,{"disambiguationData":[TD([[makeQuery(id+"F0.imprint","IMPRINT",EDGE,{"derivedFrom":subQ0}),1.0]])]});}
            extrude(context, id + "F3", {"entities" : qUnion([Q0, Q1, Q2, Q3, Q4, Q5, Q6, Q7, Q8, Q9, Q10, Q11, Q12, Q13, Q14, Q15, Q16, Q17, Q18, Q19, Q20, Q21, Q22, Q23, Q24, Q25, Q26, Q27, Q28, Q29]), "operationType" : NewBodyOperationType.ADD, "depth" : 1700 * mm, "offsetDistance" : 25 * mm});
        }
        {
            var Q0;
            {var subQ0=sQuery(id+"F0.wireOp",EDGE,"E10.left");Q0=makeQuery(id+"F0.imprint","IMPRINT",FACE,{"disambiguationData":[TD([[makeQuery(id+"F0.imprint","IMPRINT",EDGE,{"derivedFrom":subQ0}),1.0]])]});}
            var Q1;
            {var subQ0=sQuery(id+"F0.wireOp",EDGE,"E10.right");Q1=makeQuery(id+"F0.imprint","IMPRINT",FACE,{"disambiguationData":[TD([[makeQuery(id+"F0.imprint","IMPRINT",EDGE,{"derivedFrom":subQ0}),-1.0]])]});}
            var Q2;
            {var subQ0=sQuery(id+"F0.wireOp",EDGE,"E14.left");Q2=makeQuery(id+"F0.imprint","IMPRINT",FACE,{"disambiguationData":[TD([[makeQuery(id+"F0.imprint","IMPRINT",EDGE,{"derivedFrom":subQ0}),1.0]])]});}
            var Q3;
            {var subQ0=sQuery(id+"F0.wireOp",EDGE,"E14.right");Q3=makeQuery(id+"F0.imprint","IMPRINT",FACE,{"disambiguationData":[TD([[makeQuery(id+"F0.imprint","IMPRINT",EDGE,{"derivedFrom":subQ0}),-1.0]])]});}
            var Q4;
            {var subQ0=sQuery(id+"F0.wireOp",EDGE,"E23.left");Q4=makeQuery(id+"F0.imprint","IMPRINT",FACE,{"disambiguationData":[TD([[makeQuery(id+"F0.imprint","IMPRINT",EDGE,{"derivedFrom":subQ0}),1.0]])]});}
            var Q5;
            {var subQ0=sQuery(id+"F0.wireOp",EDGE,"E23.right");Q5=makeQuery(id+"F0.imprint","IMPRINT",FACE,{"disambiguationData":[TD([[makeQuery(id+"F0.imprint","IMPRINT",EDGE,{"derivedFrom":subQ0}),-1.0]])]});}
            var Q6;
            {var subQ0=sQuery(id+"F0.wireOp",EDGE,"E27.left");Q6=makeQuery(id+"F0.imprint","IMPRINT",FACE,{"disambiguationData":[TD([[makeQuery(id+"F0.imprint","IMPRINT",EDGE,{"derivedFrom":subQ0}),1.0]])]});}
            var Q7;
            {var subQ0=sQuery(id+"F0.wireOp",EDGE,"E27.right");Q7=makeQuery(id+"F0.imprint","IMPRINT",FACE,{"disambiguationData":[TD([[makeQuery(id+"F0.imprint","IMPRINT",EDGE,{"derivedFrom":subQ0}),-1.0]])]});}
            var Q8;
            {var subQ0=sQuery(id+"F0.wireOp",EDGE,"E33.left");Q8=makeQuery(id+"F0.imprint","IMPRINT",FACE,{"disambiguationData":[TD([[makeQuery(id+"F0.imprint","IMPRINT",EDGE,{"derivedFrom":subQ0}),1.0]])]});}
            var Q9;
            {var subQ0=sQuery(id+"F0.wireOp",EDGE,"E33.right");Q9=makeQuery(id+"F0.imprint","IMPRINT",FACE,{"disambiguationData":[TD([[makeQuery(id+"F0.imprint","IMPRINT",EDGE,{"derivedFrom":subQ0}),-1.0]])]});}
            var Q10;
            {var subQ0=sQuery(id+"F0.wireOp",EDGE,"E40.right");Q10=makeQuery(id+"F0.imprint","IMPRINT",FACE,{"disambiguationData":[TD([[makeQuery(id+"F0.imprint","IMPRINT",EDGE,{"derivedFrom":subQ0}),-1.0]])]});}
            var Q11;
            {var subQ0=sQuery(id+"F0.wireOp",EDGE,"E40.left");Q11=makeQuery(id+"F0.imprint","IMPRINT",FACE,{"disambiguationData":[TD([[makeQuery(id+"F0.imprint","IMPRINT",EDGE,{"derivedFrom":subQ0}),1.0]])]});}
            var Q12;
            {var subQ0=sQuery(id+"F0.wireOp",EDGE,"E30.right");Q12=makeQuery(id+"F0.imprint","IMPRINT",FACE,{"disambiguationData":[TD([[makeQuery(id+"F0.imprint","IMPRINT",EDGE,{"derivedFrom":subQ0}),-1.0]])]});}
            var Q13;
            {var subQ0=sQuery(id+"F0.wireOp",EDGE,"E36.right");Q13=makeQuery(id+"F0.imprint","IMPRINT",FACE,{"disambiguationData":[TD([[makeQuery(id+"F0.imprint","IMPRINT",EDGE,{"derivedFrom":subQ0}),-1.0]])]});}
            var Q14;
            {var subQ0=sQuery(id+"F0.wireOp",EDGE,"E36.left");Q14=makeQuery(id+"F0.imprint","IMPRINT",FACE,{"disambiguationData":[TD([[makeQuery(id+"F0.imprint","IMPRINT",EDGE,{"derivedFrom":subQ0}),1.0]])]});}
            var Q15;
            {var subQ0=sQuery(id+"F0.wireOp",EDGE,"E30.left");Q15=makeQuery(id+"F0.imprint","IMPRINT",FACE,{"disambiguationData":[TD([[makeQuery(id+"F0.imprint","IMPRINT",EDGE,{"derivedFrom":subQ0}),1.0]])]});}
            var Q16;
            {var subQ0=sQuery(id+"F0.wireOp",EDGE,"E20.right");Q16=makeQuery(id+"F0.imprint","IMPRINT",FACE,{"disambiguationData":[TD([[makeQuery(id+"F0.imprint","IMPRINT",EDGE,{"derivedFrom":subQ0}),-1.0]])]});}
            var Q17;
            {var subQ0=sQuery(id+"F0.wireOp",EDGE,"E53.right");Q17=makeQuery(id+"F0.imprint","IMPRINT",FACE,{"disambiguationData":[TD([[makeQuery(id+"F0.imprint","IMPRINT",EDGE,{"derivedFrom":subQ0}),-1.0]])]});}
            var Q18;
            {var subQ0=sQuery(id+"F0.wireOp",EDGE,"E53.left");Q18=makeQuery(id+"F0.imprint","IMPRINT",FACE,{"disambiguationData":[TD([[makeQuery(id+"F0.imprint","IMPRINT",EDGE,{"derivedFrom":subQ0}),1.0]])]});}
            var Q19;
            {var subQ0=sQuery(id+"F0.wireOp",EDGE,"E20.left");Q19=makeQuery(id+"F0.imprint","IMPRINT",FACE,{"disambiguationData":[TD([[makeQuery(id+"F0.imprint","IMPRINT",EDGE,{"derivedFrom":subQ0}),1.0]])]});}
            var Q20;
            {var subQ0=sQuery(id+"F0.wireOp",EDGE,"E17.right");Q20=makeQuery(id+"F0.imprint","IMPRINT",FACE,{"disambiguationData":[TD([[makeQuery(id+"F0.imprint","IMPRINT",EDGE,{"derivedFrom":subQ0}),-1.0]])]});}
            var Q21;
            {var subQ0=sQuery(id+"F0.wireOp",EDGE,"E49.right");Q21=makeQuery(id+"F0.imprint","IMPRINT",FACE,{"disambiguationData":[TD([[makeQuery(id+"F0.imprint","IMPRINT",EDGE,{"derivedFrom":subQ0}),-1.0]])]});}
            var Q22;
            {var subQ0=sQuery(id+"F0.wireOp",EDGE,"E49.left");Q22=makeQuery(id+"F0.imprint","IMPRINT",FACE,{"disambiguationData":[TD([[makeQuery(id+"F0.imprint","IMPRINT",EDGE,{"derivedFrom":subQ0}),1.0]])]});}
            var Q23;
            {var subQ0=sQuery(id+"F0.wireOp",EDGE,"E17.left");Q23=makeQuery(id+"F0.imprint","IMPRINT",FACE,{"disambiguationData":[TD([[makeQuery(id+"F0.imprint","IMPRINT",EDGE,{"derivedFrom":subQ0}),1.0]])]});}
            var Q24;
            {var subQ0=sQuery(id+"F0.wireOp",EDGE,"E56.left");Q24=makeQuery(id+"F0.imprint","IMPRINT",FACE,{"disambiguationData":[TD([[makeQuery(id+"F0.imprint","IMPRINT",EDGE,{"derivedFrom":subQ0}),1.0]])]});}
            var Q25;
            {var subQ0=sQuery(id+"F0.wireOp",EDGE,"E56.right");Q25=makeQuery(id+"F0.imprint","IMPRINT",FACE,{"disambiguationData":[TD([[makeQuery(id+"F0.imprint","IMPRINT",EDGE,{"derivedFrom":subQ0}),-1.0]])]});}
            var Q26;
            {var subQ0=sQuery(id+"F0.wireOp",EDGE,"E59.left");Q26=makeQuery(id+"F0.imprint","IMPRINT",FACE,{"disambiguationData":[TD([[makeQuery(id+"F0.imprint","IMPRINT",EDGE,{"derivedFrom":subQ0}),1.0]])]});}
            var Q27;
            {var subQ0=sQuery(id+"F0.wireOp",EDGE,"E59.right");Q27=makeQuery(id+"F0.imprint","IMPRINT",FACE,{"disambiguationData":[TD([[makeQuery(id+"F0.imprint","IMPRINT",EDGE,{"derivedFrom":subQ0}),-1.0]])]});}
            var Q28;
            {var subQ0=sQuery(id+"F0.wireOp",EDGE,"E43.left");Q28=makeQuery(id+"F0.imprint","IMPRINT",FACE,{"disambiguationData":[TD([[makeQuery(id+"F0.imprint","IMPRINT",EDGE,{"derivedFrom":subQ0}),1.0]])]});}
            var Q29;
            {var subQ0=sQuery(id+"F0.wireOp",EDGE,"E43.right");Q29=makeQuery(id+"F0.imprint","IMPRINT",FACE,{"disambiguationData":[TD([[makeQuery(id+"F0.imprint","IMPRINT",EDGE,{"derivedFrom":subQ0}),-1.0]])]});}
            var Q30;
            {var subQ0=sQuery(id+"F0.wireOp",EDGE,"E46.left");Q30=makeQuery(id+"F0.imprint","IMPRINT",FACE,{"disambiguationData":[TD([[makeQuery(id+"F0.imprint","IMPRINT",EDGE,{"derivedFrom":subQ0}),1.0]])]});}
            var Q31;
            {var subQ0=sQuery(id+"F0.wireOp",EDGE,"E46.right");Q31=makeQuery(id+"F0.imprint","IMPRINT",FACE,{"disambiguationData":[TD([[makeQuery(id+"F0.imprint","IMPRINT",EDGE,{"derivedFrom":subQ0}),-1.0]])]});}
            var Q32;
            {var subQ0=sQuery(id+"F0.wireOp",EDGE,"E66.right");Q32=makeQuery(id+"F0.imprint","IMPRINT",FACE,{"disambiguationData":[TD([[makeQuery(id+"F0.imprint","IMPRINT",EDGE,{"derivedFrom":subQ0}),-1.0]])]});}
            var Q33;
            {var subQ0=sQuery(id+"F0.wireOp",EDGE,"E66.left");Q33=makeQuery(id+"F0.imprint","IMPRINT",FACE,{"disambiguationData":[TD([[makeQuery(id+"F0.imprint","IMPRINT",EDGE,{"derivedFrom":subQ0}),1.0]])]});}
            var Q34;
            {var subQ0=sQuery(id+"F0.wireOp",EDGE,"E62.right");Q34=makeQuery(id+"F0.imprint","IMPRINT",FACE,{"disambiguationData":[TD([[makeQuery(id+"F0.imprint","IMPRINT",EDGE,{"derivedFrom":subQ0}),-1.0]])]});}
            var Q35;
            {var subQ0=sQuery(id+"F0.wireOp",EDGE,"E62.left");Q35=makeQuery(id+"F0.imprint","IMPRINT",FACE,{"disambiguationData":[TD([[makeQuery(id+"F0.imprint","IMPRINT",EDGE,{"derivedFrom":subQ0}),1.0]])]});}
            var Q36;
            {var subQ0=sQuery(id+"F0.wireOp",EDGE,"E79.right");Q36=makeQuery(id+"F0.imprint","IMPRINT",FACE,{"disambiguationData":[TD([[makeQuery(id+"F0.imprint","IMPRINT",EDGE,{"derivedFrom":subQ0}),-1.0]])]});}
            var Q37;
            {var subQ0=sQuery(id+"F0.wireOp",EDGE,"E79.left");Q37=makeQuery(id+"F0.imprint","IMPRINT",FACE,{"disambiguationData":[TD([[makeQuery(id+"F0.imprint","IMPRINT",EDGE,{"derivedFrom":subQ0}),1.0]])]});}
            var Q38;
            {var subQ0=sQuery(id+"F0.wireOp",EDGE,"E75.right");Q38=makeQuery(id+"F0.imprint","IMPRINT",FACE,{"disambiguationData":[TD([[makeQuery(id+"F0.imprint","IMPRINT",EDGE,{"derivedFrom":subQ0}),-1.0]])]});}
            var Q39;
            {var subQ0=sQuery(id+"F0.wireOp",EDGE,"E75.left");Q39=makeQuery(id+"F0.imprint","IMPRINT",FACE,{"disambiguationData":[TD([[makeQuery(id+"F0.imprint","IMPRINT",EDGE,{"derivedFrom":subQ0}),1.0]])]});}
            var Q40;
            {var subQ0=sQuery(id+"F0.wireOp",EDGE,"E82.left");Q40=makeQuery(id+"F0.imprint","IMPRINT",FACE,{"disambiguationData":[TD([[makeQuery(id+"F0.imprint","IMPRINT",EDGE,{"derivedFrom":subQ0}),1.0]])]});}
            var Q41;
            {var subQ0=sQuery(id+"F0.wireOp",EDGE,"E82.right");Q41=makeQuery(id+"F0.imprint","IMPRINT",FACE,{"disambiguationData":[TD([[makeQuery(id+"F0.imprint","IMPRINT",EDGE,{"derivedFrom":subQ0}),-1.0]])]});}
            var Q42;
            {var subQ0=sQuery(id+"F0.wireOp",EDGE,"E85.left");Q42=makeQuery(id+"F0.imprint","IMPRINT",FACE,{"disambiguationData":[TD([[makeQuery(id+"F0.imprint","IMPRINT",EDGE,{"derivedFrom":subQ0}),1.0]])]});}
            var Q43;
            {var subQ0=sQuery(id+"F0.wireOp",EDGE,"E85.right");Q43=makeQuery(id+"F0.imprint","IMPRINT",FACE,{"disambiguationData":[TD([[makeQuery(id+"F0.imprint","IMPRINT",EDGE,{"derivedFrom":subQ0}),-1.0]])]});}
            var Q44;
            {var subQ0=sQuery(id+"F0.wireOp",EDGE,"E69.left");Q44=makeQuery(id+"F0.imprint","IMPRINT",FACE,{"disambiguationData":[TD([[makeQuery(id+"F0.imprint","IMPRINT",EDGE,{"derivedFrom":subQ0}),1.0]])]});}
            var Q45;
            {var subQ0=sQuery(id+"F0.wireOp",EDGE,"E69.right");Q45=makeQuery(id+"F0.imprint","IMPRINT",FACE,{"disambiguationData":[TD([[makeQuery(id+"F0.imprint","IMPRINT",EDGE,{"derivedFrom":subQ0}),-1.0]])]});}
            var Q46;
            {var subQ0=sQuery(id+"F0.wireOp",EDGE,"E72.left");Q46=makeQuery(id+"F0.imprint","IMPRINT",FACE,{"disambiguationData":[TD([[makeQuery(id+"F0.imprint","IMPRINT",EDGE,{"derivedFrom":subQ0}),1.0]])]});}
            var Q47;
            {var subQ0=sQuery(id+"F0.wireOp",EDGE,"E72.right");Q47=makeQuery(id+"F0.imprint","IMPRINT",FACE,{"disambiguationData":[TD([[makeQuery(id+"F0.imprint","IMPRINT",EDGE,{"derivedFrom":subQ0}),-1.0]])]});}
            var Q48;
            {var subQ0=sQuery(id+"F0.wireOp",EDGE,"E106.right");Q48=makeQuery(id+"F0.imprint","IMPRINT",FACE,{"disambiguationData":[TD([[makeQuery(id+"F0.imprint","IMPRINT",EDGE,{"derivedFrom":subQ0}),-1.0]])]});}
            var Q49;
            {var subQ0=sQuery(id+"F0.wireOp",EDGE,"E106.left");Q49=makeQuery(id+"F0.imprint","IMPRINT",FACE,{"disambiguationData":[TD([[makeQuery(id+"F0.imprint","IMPRINT",EDGE,{"derivedFrom":subQ0}),1.0]])]});}
            var Q50;
            {var subQ0=sQuery(id+"F0.wireOp",EDGE,"E102.right");Q50=makeQuery(id+"F0.imprint","IMPRINT",FACE,{"disambiguationData":[TD([[makeQuery(id+"F0.imprint","IMPRINT",EDGE,{"derivedFrom":subQ0}),-1.0]])]});}
            var Q51;
            {var subQ0=sQuery(id+"F0.wireOp",EDGE,"E102.left");Q51=makeQuery(id+"F0.imprint","IMPRINT",FACE,{"disambiguationData":[TD([[makeQuery(id+"F0.imprint","IMPRINT",EDGE,{"derivedFrom":subQ0}),1.0]])]});}
            var Q52;
            {var subQ0=sQuery(id+"F0.wireOp",EDGE,"E99.right");Q52=makeQuery(id+"F0.imprint","IMPRINT",FACE,{"disambiguationData":[TD([[makeQuery(id+"F0.imprint","IMPRINT",EDGE,{"derivedFrom":subQ0}),-1.0]])]});}
            var Q53;
            {var subQ0=sQuery(id+"F0.wireOp",EDGE,"E99.left");Q53=makeQuery(id+"F0.imprint","IMPRINT",FACE,{"disambiguationData":[TD([[makeQuery(id+"F0.imprint","IMPRINT",EDGE,{"derivedFrom":subQ0}),1.0]])]});}
            var Q54;
            {var subQ0=sQuery(id+"F0.wireOp",EDGE,"E95.right");Q54=makeQuery(id+"F0.imprint","IMPRINT",FACE,{"disambiguationData":[TD([[makeQuery(id+"F0.imprint","IMPRINT",EDGE,{"derivedFrom":subQ0}),-1.0]])]});}
            var Q55;
            {var subQ0=sQuery(id+"F0.wireOp",EDGE,"E95.left");Q55=makeQuery(id+"F0.imprint","IMPRINT",FACE,{"disambiguationData":[TD([[makeQuery(id+"F0.imprint","IMPRINT",EDGE,{"derivedFrom":subQ0}),1.0]])]});}
            var Q56;
            {var subQ0=sQuery(id+"F0.wireOp",EDGE,"E92.right");Q56=makeQuery(id+"F0.imprint","IMPRINT",FACE,{"disambiguationData":[TD([[makeQuery(id+"F0.imprint","IMPRINT",EDGE,{"derivedFrom":subQ0}),-1.0]])]});}
            var Q57;
            {var subQ0=sQuery(id+"F0.wireOp",EDGE,"E92.left");Q57=makeQuery(id+"F0.imprint","IMPRINT",FACE,{"disambiguationData":[TD([[makeQuery(id+"F0.imprint","IMPRINT",EDGE,{"derivedFrom":subQ0}),1.0]])]});}
            var Q58;
            {var subQ0=sQuery(id+"F0.wireOp",EDGE,"E88.left");Q58=makeQuery(id+"F0.imprint","IMPRINT",FACE,{"disambiguationData":[TD([[makeQuery(id+"F0.imprint","IMPRINT",EDGE,{"derivedFrom":subQ0}),1.0]])]});}
            var Q59;
            {var subQ0=sQuery(id+"F0.wireOp",EDGE,"E88.right");Q59=makeQuery(id+"F0.imprint","IMPRINT",FACE,{"disambiguationData":[TD([[makeQuery(id+"F0.imprint","IMPRINT",EDGE,{"derivedFrom":subQ0}),-1.0]])]});}
            extrude(context, id + "F4", {"entities" : qUnion([Q0, Q1, Q2, Q3, Q4, Q5, Q6, Q7, Q8, Q9, Q10, Q11, Q12, Q13, Q14, Q15, Q16, Q17, Q18, Q19, Q20, Q21, Q22, Q23, Q24, Q25, Q26, Q27, Q28, Q29, Q30, Q31, Q32, Q33, Q34, Q35, Q36, Q37, Q38, Q39, Q40, Q41, Q42, Q43, Q44, Q45, Q46, Q47, Q48, Q49, Q50, Q51, Q52, Q53, Q54, Q55, Q56, Q57, Q58, Q59]), "operationType" : NewBodyOperationType.ADD, "depth" : 100 * mm, "offsetDistance" : 25 * mm});
        }
        {
            var Q0;
            Q0=makeQuery(id+"F0.imprint","IMPRINT",FACE,{"disambiguationData":[TD([[makeQuery(id+"F0.imprint","IMPRINT",EDGE,{"derivedFrom":sQuery(id+"F0.wireOp",EDGE,"E13.bottom")}),-1.0]])]});
            var Q1;
            Q1=makeQuery(id+"F0.imprint","IMPRINT",FACE,{"disambiguationData":[TD([[makeQuery(id+"F0.imprint","IMPRINT",EDGE,{"derivedFrom":sQuery(id+"F0.wireOp",EDGE,"E26.bottom")}),-1.0]])]});
            var Q2;
            Q2=makeQuery(id+"F0.imprint","IMPRINT",FACE,{"disambiguationData":[TD([[makeQuery(id+"F0.imprint","IMPRINT",EDGE,{"derivedFrom":sQuery(id+"F0.wireOp",EDGE,"E39.bottom")}),-1.0]])]});
            var Q3;
            Q3=makeQuery(id+"F0.imprint","IMPRINT",FACE,{"disambiguationData":[TD([[makeQuery(id+"F0.imprint","IMPRINT",EDGE,{"derivedFrom":sQuery(id+"F0.wireOp",EDGE,"E52.bottom")}),-1.0]])]});
            var Q4;
            Q4=makeQuery(id+"F0.imprint","IMPRINT",FACE,{"disambiguationData":[TD([[makeQuery(id+"F0.imprint","IMPRINT",EDGE,{"derivedFrom":sQuery(id+"F0.wireOp",EDGE,"E78.bottom")}),-1.0]])]});
            var Q5;
            Q5=makeQuery(id+"F0.imprint","IMPRINT",FACE,{"disambiguationData":[TD([[makeQuery(id+"F0.imprint","IMPRINT",EDGE,{"derivedFrom":sQuery(id+"F0.wireOp",EDGE,"E65.bottom")}),-1.0]])]});
            var Q6;
            Q6=makeQuery(id+"F0.imprint","IMPRINT",FACE,{"disambiguationData":[TD([[makeQuery(id+"F0.imprint","IMPRINT",EDGE,{"derivedFrom":sQuery(id+"F0.wireOp",EDGE,"E105.bottom")}),-1.0]])]});
            var Q7;
            Q7=makeQuery(id+"F0.imprint","IMPRINT",FACE,{"disambiguationData":[TD([[makeQuery(id+"F0.imprint","IMPRINT",EDGE,{"derivedFrom":sQuery(id+"F0.wireOp",EDGE,"E98.bottom")}),-1.0]])]});
            var Q8;
            Q8=makeQuery(id+"F0.imprint","IMPRINT",FACE,{"disambiguationData":[TD([[makeQuery(id+"F0.imprint","IMPRINT",EDGE,{"derivedFrom":sQuery(id+"F0.wireOp",EDGE,"E91.bottom")}),-1.0]])]});
            extrude(context, id + "F5", {"entities" : qUnion([Q0, Q1, Q2, Q3, Q4, Q5, Q6, Q7, Q8]), "operationType" : NewBodyOperationType.ADD, "depth" : 2000 * mm, "offsetDistance" : 25 * mm});
        }
        {
            var Q0;
            Q0=makeQuery(id+"F3.opExtrude","CAP_EDGE",EDGE,{"disambiguationData":[OSD([sQuery(id+"F0.wireOp",EDGE,"E11")])],"isStart":false});
            var Q1;
            Q1=makeQuery(id+"F3.opExtrude","CAP_EDGE",EDGE,{"disambiguationData":[OSD([sQuery(id+"F0.wireOp",EDGE,"E12")])],"isStart":false});
            chamfer(context, id + "F6", {"entities" : qUnion([Q0, Q1]), "chamferType" : ChamferType.OFFSET_ANGLE, "width" : 400 * mm, "oppositeDirection" : false, "angle" : 70 * degree});
        }
        {
            var Q0;
            Q0=makeQuery(id+"F3.opExtrude","CAP_EDGE",EDGE,{"disambiguationData":[OSD([sQuery(id+"F0.wireOp",EDGE,"E15")])],"isStart":false});
            var Q1;
            Q1=makeQuery(id+"F3.opExtrude","CAP_EDGE",EDGE,{"disambiguationData":[OSD([sQuery(id+"F0.wireOp",EDGE,"E16")])],"isStart":false});
            chamfer(context, id + "F7", {"entities" : qUnion([Q0, Q1]), "chamferType" : ChamferType.OFFSET_ANGLE, "width" : 400 * mm, "oppositeDirection" : false, "angle" : 70 * degree, "tangentPropagation" : true});
        }
        {
            var Q0;
            Q0=makeQuery(id+"F3.opExtrude","CAP_EDGE",EDGE,{"disambiguationData":[OSD([sQuery(id+"F0.wireOp",EDGE,"E24")])],"isStart":false});
            var Q1;
            Q1=makeQuery(id+"F3.opExtrude","CAP_EDGE",EDGE,{"disambiguationData":[OSD([sQuery(id+"F0.wireOp",EDGE,"E25")])],"isStart":false});
            chamfer(context, id + "F8", {"entities" : qUnion([Q0, Q1]), "chamferType" : ChamferType.OFFSET_ANGLE, "width" : 400 * mm, "oppositeDirection" : false, "angle" : 70 * degree, "tangentPropagation" : true});
        }
        {
            var Q0;
            Q0=makeQuery(id+"F3.opExtrude","CAP_EDGE",EDGE,{"disambiguationData":[OSD([sQuery(id+"F0.wireOp",EDGE,"E28")])],"isStart":false});
            var Q1;
            Q1=makeQuery(id+"F3.opExtrude","CAP_EDGE",EDGE,{"disambiguationData":[OSD([sQuery(id+"F0.wireOp",EDGE,"E29")])],"isStart":false});
            chamfer(context, id + "F9", {"entities" : qUnion([Q0, Q1]), "chamferType" : ChamferType.OFFSET_ANGLE, "width" : 400 * mm, "oppositeDirection" : false, "angle" : 70 * degree, "tangentPropagation" : true});
        }
        {
            var Q0;
            Q0=makeQuery(id+"F3.opExtrude","CAP_EDGE",EDGE,{"disambiguationData":[OSD([sQuery(id+"F0.wireOp",EDGE,"E18")])],"isStart":false});
            var Q1;
            Q1=makeQuery(id+"F3.opExtrude","CAP_EDGE",EDGE,{"disambiguationData":[OSD([sQuery(id+"F0.wireOp",EDGE,"E19")])],"isStart":false});
            chamfer(context, id + "F10", {"entities" : qUnion([Q0, Q1]), "chamferType" : ChamferType.OFFSET_ANGLE, "width" : 400 * mm, "oppositeDirection" : false, "angle" : 70 * degree, "tangentPropagation" : true});
        }
        {
            var Q0;
            Q0=makeQuery(id+"F3.opExtrude","CAP_EDGE",EDGE,{"disambiguationData":[OSD([sQuery(id+"F0.wireOp",EDGE,"E21")])],"isStart":false});
            var Q1;
            Q1=makeQuery(id+"F3.opExtrude","CAP_EDGE",EDGE,{"disambiguationData":[OSD([sQuery(id+"F0.wireOp",EDGE,"E22")])],"isStart":false});
            chamfer(context, id + "F11", {"entities" : qUnion([Q0, Q1]), "chamferType" : ChamferType.OFFSET_ANGLE, "width" : 400 * mm, "oppositeDirection" : false, "angle" : 70 * degree, "tangentPropagation" : true});
        }
        {
            var Q0;
            Q0=makeQuery(id+"F3.opExtrude","CAP_EDGE",EDGE,{"disambiguationData":[OSD([sQuery(id+"F0.wireOp",EDGE,"E31")])],"isStart":false});
            var Q1;
            Q1=makeQuery(id+"F3.opExtrude","CAP_EDGE",EDGE,{"disambiguationData":[OSD([sQuery(id+"F0.wireOp",EDGE,"E32")])],"isStart":false});
            chamfer(context, id + "F12", {"entities" : qUnion([Q0, Q1]), "chamferType" : ChamferType.OFFSET_ANGLE, "width" : 400 * mm, "oppositeDirection" : false, "angle" : 70 * degree, "tangentPropagation" : true});
        }
        {
            var Q0;
            Q0=makeQuery(id+"F3.opExtrude","CAP_EDGE",EDGE,{"disambiguationData":[OSD([sQuery(id+"F0.wireOp",EDGE,"E34")])],"isStart":false});
            var Q1;
            Q1=makeQuery(id+"F3.opExtrude","CAP_EDGE",EDGE,{"disambiguationData":[OSD([sQuery(id+"F0.wireOp",EDGE,"E35")])],"isStart":false});
            chamfer(context, id + "F13", {"entities" : qUnion([Q0, Q1]), "chamferType" : ChamferType.OFFSET_ANGLE, "width" : 400 * mm, "oppositeDirection" : false, "angle" : 70 * degree, "tangentPropagation" : true});
        }
        {
            var Q0;
            Q0=makeQuery(id+"F3.opExtrude","CAP_EDGE",EDGE,{"disambiguationData":[OSD([sQuery(id+"F0.wireOp",EDGE,"E50")])],"isStart":false});
            var Q1;
            Q1=makeQuery(id+"F3.opExtrude","CAP_EDGE",EDGE,{"disambiguationData":[OSD([sQuery(id+"F0.wireOp",EDGE,"E51")])],"isStart":false});
            chamfer(context, id + "F14", {"entities" : qUnion([Q0, Q1]), "chamferType" : ChamferType.OFFSET_ANGLE, "width" : 400 * mm, "oppositeDirection" : false, "angle" : 70 * degree, "tangentPropagation" : true});
        }
        {
            var Q0;
            Q0=makeQuery(id+"F3.opExtrude","CAP_EDGE",EDGE,{"disambiguationData":[OSD([sQuery(id+"F0.wireOp",EDGE,"E54")])],"isStart":false});
            var Q1;
            Q1=makeQuery(id+"F3.opExtrude","CAP_EDGE",EDGE,{"disambiguationData":[OSD([sQuery(id+"F0.wireOp",EDGE,"E55")])],"isStart":false});
            chamfer(context, id + "F15", {"entities" : qUnion([Q0, Q1]), "chamferType" : ChamferType.OFFSET_ANGLE, "width" : 400 * mm, "oppositeDirection" : false, "angle" : 70 * degree, "tangentPropagation" : true});
        }
        {
            var Q0;
            Q0=makeQuery(id+"F3.opExtrude","CAP_EDGE",EDGE,{"disambiguationData":[OSD([sQuery(id+"F0.wireOp",EDGE,"E37")])],"isStart":false});
            var Q1;
            Q1=makeQuery(id+"F3.opExtrude","CAP_EDGE",EDGE,{"disambiguationData":[OSD([sQuery(id+"F0.wireOp",EDGE,"E38")])],"isStart":false});
            chamfer(context, id + "F16", {"entities" : qUnion([Q0, Q1]), "chamferType" : ChamferType.OFFSET_ANGLE, "width" : 400 * mm, "oppositeDirection" : false, "angle" : 70 * degree, "tangentPropagation" : true});
        }
        {
            var Q0;
            Q0=makeQuery(id+"F3.opExtrude","CAP_EDGE",EDGE,{"disambiguationData":[OSD([sQuery(id+"F0.wireOp",EDGE,"E41")])],"isStart":false});
            var Q1;
            Q1=makeQuery(id+"F3.opExtrude","CAP_EDGE",EDGE,{"disambiguationData":[OSD([sQuery(id+"F0.wireOp",EDGE,"E42")])],"isStart":false});
            chamfer(context, id + "F17", {"entities" : qUnion([Q0, Q1]), "chamferType" : ChamferType.OFFSET_ANGLE, "width" : 400 * mm, "oppositeDirection" : false, "angle" : 70 * degree, "tangentPropagation" : true});
        }
        {
            var Q0;
            Q0=makeQuery(id+"F3.opExtrude","CAP_EDGE",EDGE,{"disambiguationData":[OSD([sQuery(id+"F0.wireOp",EDGE,"E89")])],"isStart":false});
            var Q1;
            Q1=makeQuery(id+"F3.opExtrude","CAP_EDGE",EDGE,{"disambiguationData":[OSD([sQuery(id+"F0.wireOp",EDGE,"E90")])],"isStart":false});
            chamfer(context, id + "F18", {"entities" : qUnion([Q0, Q1]), "chamferType" : ChamferType.OFFSET_ANGLE, "width" : 400 * mm, "oppositeDirection" : false, "angle" : 70 * degree, "tangentPropagation" : true});
        }
        {
            var Q0;
            Q0=makeQuery(id+"F3.opExtrude","CAP_EDGE",EDGE,{"disambiguationData":[OSD([sQuery(id+"F0.wireOp",EDGE,"E93")])],"isStart":false});
            var Q1;
            Q1=makeQuery(id+"F3.opExtrude","CAP_EDGE",EDGE,{"disambiguationData":[OSD([sQuery(id+"F0.wireOp",EDGE,"E94")])],"isStart":false});
            chamfer(context, id + "F19", {"entities" : qUnion([Q0, Q1]), "chamferType" : ChamferType.OFFSET_ANGLE, "width" : 400 * mm, "oppositeDirection" : false, "angle" : 70 * degree, "tangentPropagation" : true});
        }
        {
            var Q0;
            Q0=makeQuery(id+"F3.opExtrude","CAP_EDGE",EDGE,{"disambiguationData":[OSD([sQuery(id+"F0.wireOp",EDGE,"E57")])],"isStart":false});
            var Q1;
            Q1=makeQuery(id+"F3.opExtrude","CAP_EDGE",EDGE,{"disambiguationData":[OSD([sQuery(id+"F0.wireOp",EDGE,"E58")])],"isStart":false});
            chamfer(context, id + "F20", {"entities" : qUnion([Q0, Q1]), "chamferType" : ChamferType.OFFSET_ANGLE, "width" : 400 * mm, "oppositeDirection" : false, "angle" : 70 * degree, "tangentPropagation" : true});
        }
        {
            var Q0;
            Q0=makeQuery(id+"F3.opExtrude","CAP_EDGE",EDGE,{"disambiguationData":[OSD([sQuery(id+"F0.wireOp",EDGE,"E60")])],"isStart":false});
            var Q1;
            Q1=makeQuery(id+"F3.opExtrude","CAP_EDGE",EDGE,{"disambiguationData":[OSD([sQuery(id+"F0.wireOp",EDGE,"E61")])],"isStart":false});
            chamfer(context, id + "F21", {"entities" : qUnion([Q0, Q1]), "chamferType" : ChamferType.OFFSET_ANGLE, "width" : 400 * mm, "oppositeDirection" : false, "angle" : 70 * degree, "tangentPropagation" : true});
        }
        {
            var Q0;
            Q0=makeQuery(id+"F3.opExtrude","CAP_EDGE",EDGE,{"disambiguationData":[OSD([sQuery(id+"F0.wireOp",EDGE,"E44")])],"isStart":false});
            var Q1;
            Q1=makeQuery(id+"F3.opExtrude","CAP_EDGE",EDGE,{"disambiguationData":[OSD([sQuery(id+"F0.wireOp",EDGE,"E45")])],"isStart":false});
            chamfer(context, id + "F22", {"entities" : qUnion([Q0, Q1]), "chamferType" : ChamferType.OFFSET_ANGLE, "width" : 400 * mm, "oppositeDirection" : false, "angle" : 70 * degree, "tangentPropagation" : true});
        }
        {
            var Q0;
            Q0=makeQuery(id+"F3.opExtrude","CAP_EDGE",EDGE,{"disambiguationData":[OSD([sQuery(id+"F0.wireOp",EDGE,"E47")])],"isStart":false});
            var Q1;
            Q1=makeQuery(id+"F3.opExtrude","CAP_EDGE",EDGE,{"disambiguationData":[OSD([sQuery(id+"F0.wireOp",EDGE,"E48")])],"isStart":false});
            chamfer(context, id + "F23", {"entities" : qUnion([Q0, Q1]), "chamferType" : ChamferType.OFFSET_ANGLE, "width" : 400 * mm, "oppositeDirection" : false, "angle" : 70 * degree, "tangentPropagation" : true});
        }
        {
            var Q0;
            Q0=makeQuery(id+"F3.opExtrude","CAP_EDGE",EDGE,{"disambiguationData":[OSD([sQuery(id+"F0.wireOp",EDGE,"E76")])],"isStart":false});
            var Q1;
            Q1=makeQuery(id+"F3.opExtrude","CAP_EDGE",EDGE,{"disambiguationData":[OSD([sQuery(id+"F0.wireOp",EDGE,"E77")])],"isStart":false});
            chamfer(context, id + "F24", {"entities" : qUnion([Q0, Q1]), "chamferType" : ChamferType.OFFSET_ANGLE, "width" : 400 * mm, "oppositeDirection" : false, "angle" : 70 * degree, "tangentPropagation" : true});
        }
        {
            var Q0;
            Q0=makeQuery(id+"F3.opExtrude","CAP_EDGE",EDGE,{"disambiguationData":[OSD([sQuery(id+"F0.wireOp",EDGE,"E80")])],"isStart":false});
            var Q1;
            Q1=makeQuery(id+"F3.opExtrude","CAP_EDGE",EDGE,{"disambiguationData":[OSD([sQuery(id+"F0.wireOp",EDGE,"E81")])],"isStart":false});
            chamfer(context, id + "F25", {"entities" : qUnion([Q0, Q1]), "chamferType" : ChamferType.OFFSET_ANGLE, "width" : 400 * mm, "oppositeDirection" : false, "angle" : 70 * degree, "tangentPropagation" : true});
        }
        {
            var Q0;
            Q0=makeQuery(id+"F3.opExtrude","CAP_EDGE",EDGE,{"disambiguationData":[OSD([sQuery(id+"F0.wireOp",EDGE,"E63")])],"isStart":false});
            var Q1;
            Q1=makeQuery(id+"F3.opExtrude","CAP_EDGE",EDGE,{"disambiguationData":[OSD([sQuery(id+"F0.wireOp",EDGE,"E64")])],"isStart":false});
            chamfer(context, id + "F26", {"entities" : qUnion([Q0, Q1]), "chamferType" : ChamferType.OFFSET_ANGLE, "width" : 400 * mm, "oppositeDirection" : false, "angle" : 70 * degree, "tangentPropagation" : true});
        }
        {
            var Q0;
            Q0=makeQuery(id+"F3.opExtrude","CAP_EDGE",EDGE,{"disambiguationData":[OSD([sQuery(id+"F0.wireOp",EDGE,"E67")])],"isStart":false});
            var Q1;
            Q1=makeQuery(id+"F3.opExtrude","CAP_EDGE",EDGE,{"disambiguationData":[OSD([sQuery(id+"F0.wireOp",EDGE,"E68")])],"isStart":false});
            chamfer(context, id + "F27", {"entities" : qUnion([Q0, Q1]), "chamferType" : ChamferType.OFFSET_ANGLE, "width" : 400 * mm, "oppositeDirection" : false, "angle" : 70 * degree, "tangentPropagation" : true});
        }
        {
            var Q0;
            Q0=makeQuery(id+"F3.opExtrude","CAP_EDGE",EDGE,{"disambiguationData":[OSD([sQuery(id+"F0.wireOp",EDGE,"E83")])],"isStart":false});
            var Q1;
            Q1=makeQuery(id+"F3.opExtrude","CAP_EDGE",EDGE,{"disambiguationData":[OSD([sQuery(id+"F0.wireOp",EDGE,"E84")])],"isStart":false});
            chamfer(context, id + "F28", {"entities" : qUnion([Q0, Q1]), "chamferType" : ChamferType.OFFSET_ANGLE, "width" : 400 * mm, "oppositeDirection" : false, "angle" : 70 * degree, "tangentPropagation" : true});
        }
        {
            var Q0;
            Q0=makeQuery(id+"F3.opExtrude","CAP_EDGE",EDGE,{"disambiguationData":[OSD([sQuery(id+"F0.wireOp",EDGE,"E86")])],"isStart":false});
            var Q1;
            Q1=makeQuery(id+"F3.opExtrude","CAP_EDGE",EDGE,{"disambiguationData":[OSD([sQuery(id+"F0.wireOp",EDGE,"E87")])],"isStart":false});
            chamfer(context, id + "F29", {"entities" : qUnion([Q0, Q1]), "chamferType" : ChamferType.OFFSET_ANGLE, "width" : 400 * mm, "oppositeDirection" : false, "angle" : 70 * degree, "tangentPropagation" : true});
        }
        {
            var Q0;
            Q0=makeQuery(id+"F3.opExtrude","CAP_EDGE",EDGE,{"disambiguationData":[OSD([sQuery(id+"F0.wireOp",EDGE,"E70")])],"isStart":false});
            var Q1;
            Q1=makeQuery(id+"F3.opExtrude","CAP_EDGE",EDGE,{"disambiguationData":[OSD([sQuery(id+"F0.wireOp",EDGE,"E71")])],"isStart":false});
            chamfer(context, id + "F30", {"entities" : qUnion([Q0, Q1]), "chamferType" : ChamferType.OFFSET_ANGLE, "width" : 400 * mm, "oppositeDirection" : false, "angle" : 70 * degree, "tangentPropagation" : true});
        }
        {
            var Q0;
            Q0=makeQuery(id+"F3.opExtrude","CAP_EDGE",EDGE,{"disambiguationData":[OSD([sQuery(id+"F0.wireOp",EDGE,"E73")])],"isStart":false});
            var Q1;
            Q1=makeQuery(id+"F3.opExtrude","CAP_EDGE",EDGE,{"disambiguationData":[OSD([sQuery(id+"F0.wireOp",EDGE,"E74")])],"isStart":false});
            chamfer(context, id + "F31", {"entities" : qUnion([Q0, Q1]), "chamferType" : ChamferType.OFFSET_ANGLE, "width" : 400 * mm, "oppositeDirection" : false, "angle" : 70 * degree, "tangentPropagation" : true});
        }
        {
            var Q0;
            Q0=makeQuery(id+"F3.opExtrude","CAP_EDGE",EDGE,{"disambiguationData":[OSD([sQuery(id+"F0.wireOp",EDGE,"E96")])],"isStart":false});
            var Q1;
            Q1=makeQuery(id+"F3.opExtrude","CAP_EDGE",EDGE,{"disambiguationData":[OSD([sQuery(id+"F0.wireOp",EDGE,"E97")])],"isStart":false});
            chamfer(context, id + "F32", {"entities" : qUnion([Q0, Q1]), "chamferType" : ChamferType.OFFSET_ANGLE, "width" : 400 * mm, "oppositeDirection" : false, "angle" : 70 * degree, "tangentPropagation" : true});
        }
        {
            var Q0;
            Q0=makeQuery(id+"F3.opExtrude","CAP_EDGE",EDGE,{"disambiguationData":[OSD([sQuery(id+"F0.wireOp",EDGE,"E100")])],"isStart":false});
            var Q1;
            Q1=makeQuery(id+"F3.opExtrude","CAP_EDGE",EDGE,{"disambiguationData":[OSD([sQuery(id+"F0.wireOp",EDGE,"E101")])],"isStart":false});
            chamfer(context, id + "F33", {"entities" : qUnion([Q0, Q1]), "chamferType" : ChamferType.OFFSET_ANGLE, "width" : 400 * mm, "oppositeDirection" : false, "angle" : 70 * degree, "tangentPropagation" : true});
        }
        {
            var Q0;
            Q0=makeQuery(id+"F3.opExtrude","CAP_EDGE",EDGE,{"disambiguationData":[OSD([sQuery(id+"F0.wireOp",EDGE,"E103")])],"isStart":false});
            var Q1;
            Q1=makeQuery(id+"F3.opExtrude","CAP_EDGE",EDGE,{"disambiguationData":[OSD([sQuery(id+"F0.wireOp",EDGE,"E104")])],"isStart":false});
            chamfer(context, id + "F34", {"entities" : qUnion([Q0, Q1]), "chamferType" : ChamferType.OFFSET_ANGLE, "width" : 400 * mm, "oppositeDirection" : false, "angle" : 70 * degree, "tangentPropagation" : true});
        }
        {
            var Q0;
            Q0=makeQuery(id+"F3.opExtrude","CAP_EDGE",EDGE,{"disambiguationData":[OSD([sQuery(id+"F0.wireOp",EDGE,"E107")])],"isStart":false});
            var Q1;
            Q1=makeQuery(id+"F3.opExtrude","CAP_EDGE",EDGE,{"disambiguationData":[OSD([sQuery(id+"F0.wireOp",EDGE,"E108")])],"isStart":false});
            chamfer(context, id + "F35", {"entities" : qUnion([Q0, Q1]), "chamferType" : ChamferType.OFFSET_ANGLE, "width" : 400 * mm, "oppositeDirection" : false, "angle" : 70 * degree, "tangentPropagation" : true});
        }
        {
            var Q0;
            Q0=makeQuery(id+"F0.imprint","IMPRINT",FACE,{"disambiguationData":[TD([[makeQuery(id+"F0.imprint","IMPRINT",EDGE,{"derivedFrom":sQuery(id+"F0.wireOp",EDGE,"E109.bottom")}),-1.0]])]});
            extrude(context, id + "F36", {"entities" : qUnion([Q0]), "operationType" : NewBodyOperationType.ADD, "depth" : 500 * mm, "offsetDistance" : 25 * mm});
        }
    });
